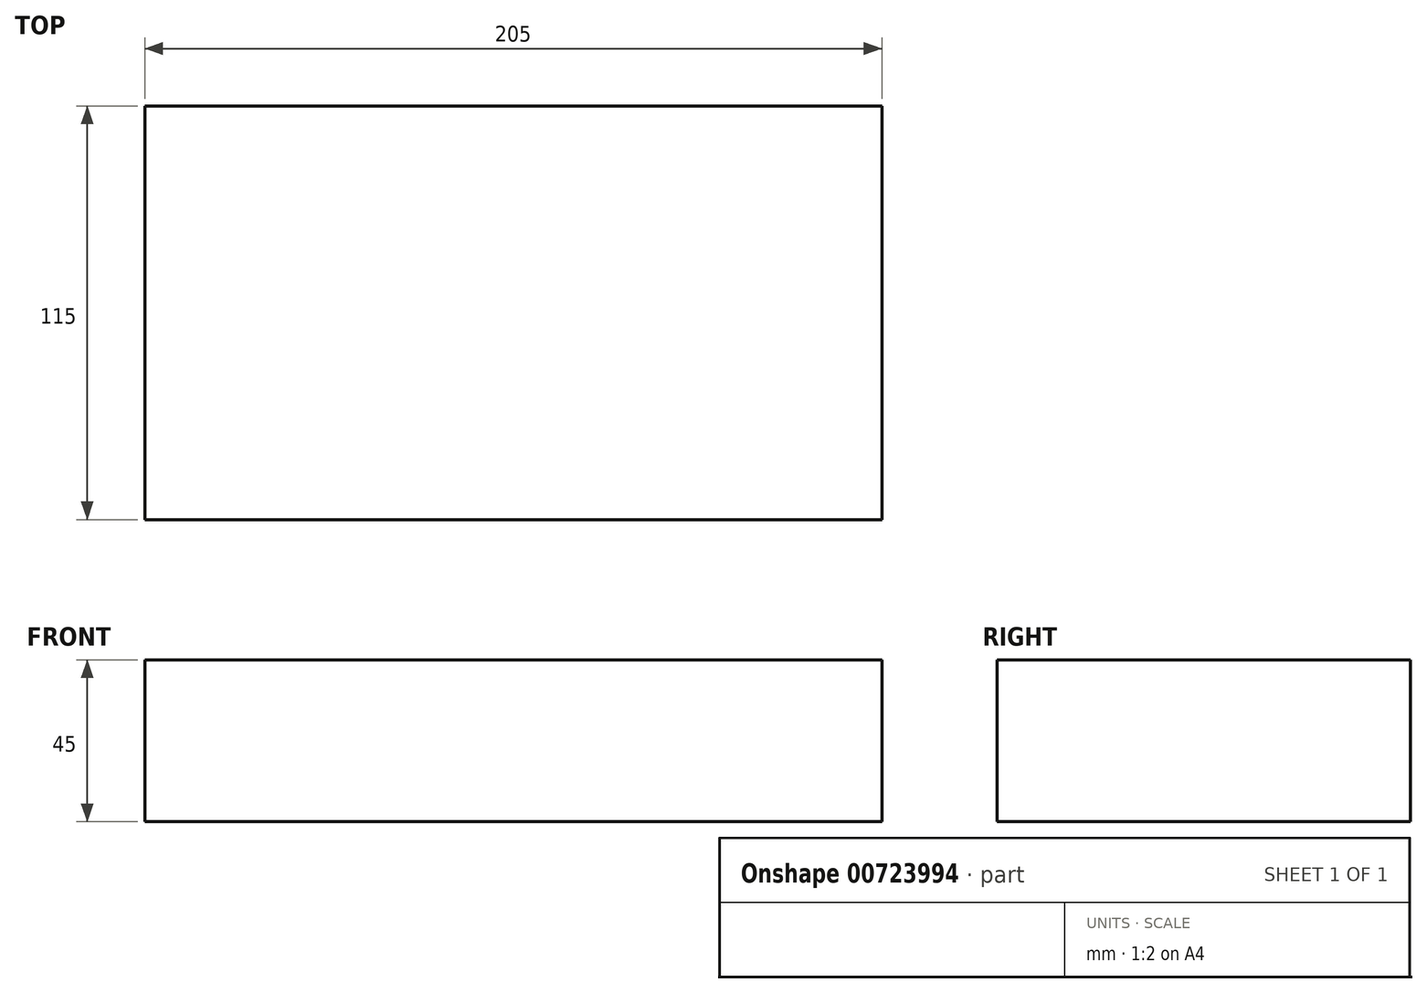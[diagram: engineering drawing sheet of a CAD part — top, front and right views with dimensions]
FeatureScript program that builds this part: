
annotation { "Feature Type Name" : "Feature", "Feature Type Description" : "" }
export const myFeature = defineFeature(function(context is Context, id is Id, definition is map)
    precondition{}
    {
        {
            var Q0;
            Q0=qCreatedBy(makeId("Top.planeOp"),FACE);
            var sketch = newSketch(context, id + "F0", { "sketchPlane" : qUnion([Q0])});
            skLineSegment(sketch, "E0.bottom", {"start": v(-102.5, 57.5) * mm, "end": v(102.5, 57.5) * mm});
            skLineSegment(sketch, "E0.top", {"start": v(-102.5, -57.5) * mm, "end": v(102.5, -57.5) * mm});
            skLineSegment(sketch, "E0.left", {"start": v(-102.5, 57.5) * mm, "end": v(-102.5, -57.5) * mm});
            skLineSegment(sketch, "E0.right", {"start": v(102.5, 57.5) * mm, "end": v(102.5, -57.5) * mm});
            skLineSegment(sketch, "E1", {"start": v(-102.5, 57.5) * mm, "end": v(102.5, -57.5) * mm, "construction": true});
            skLineSegment(sketch, "E2", {"start": v(102.5, 57.5) * mm, "end": v(-102.5, -57.5) * mm, "construction": true});
            skSolve(sketch);
        }
        {
            var Q0;
            Q0=qSketchRegion(id+"F0",true);
            extrude(context, id + "F1", {"entities" : qUnion([Q0]), "depth" : 45 * mm, "offsetDistance" : 25 * mm});
        }
    });
